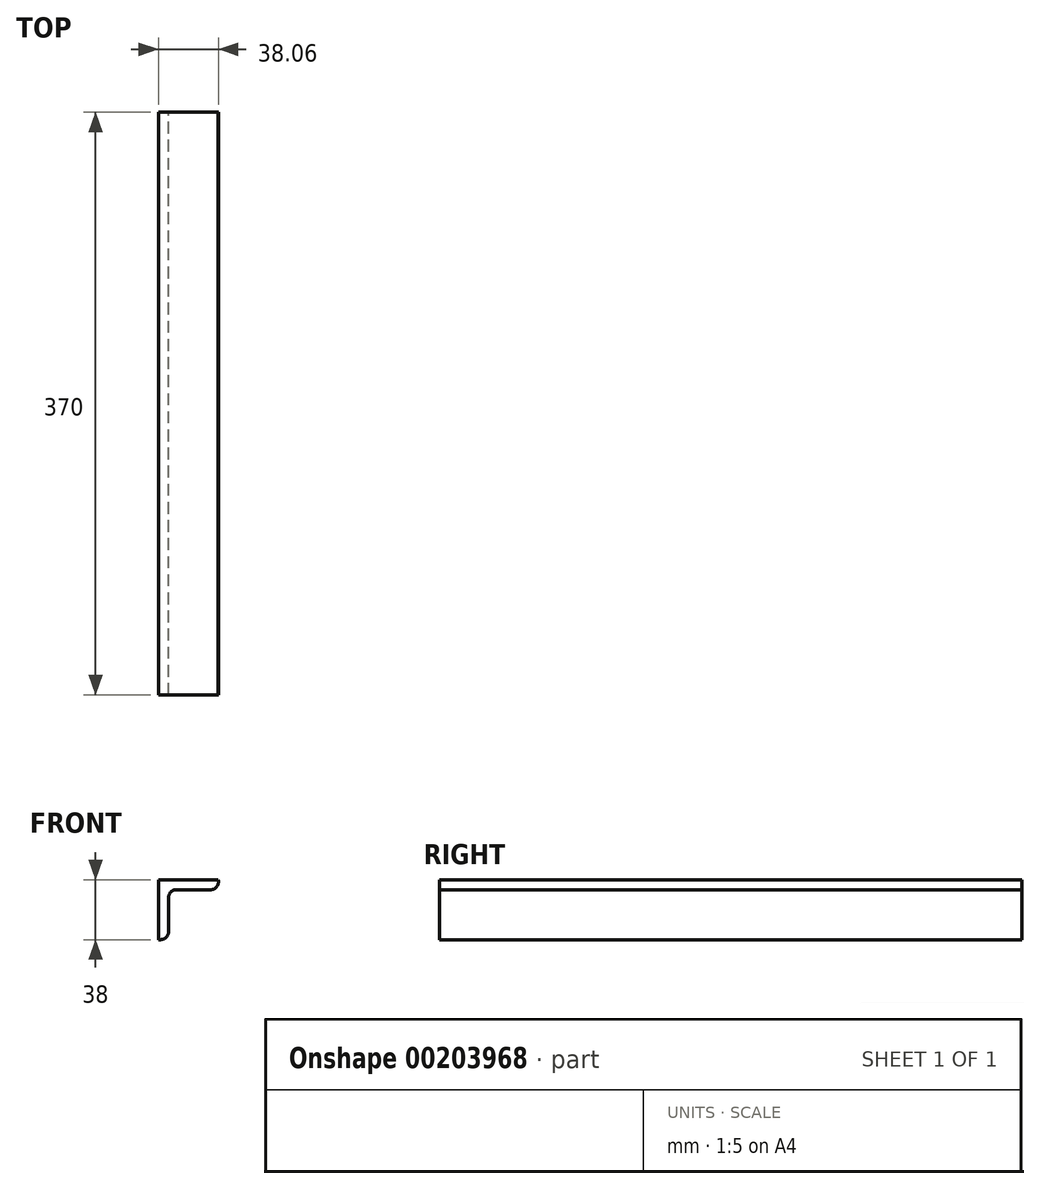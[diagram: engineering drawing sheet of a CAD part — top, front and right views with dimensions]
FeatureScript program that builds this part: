
annotation { "Feature Type Name" : "Feature", "Feature Type Description" : "" }
export const myFeature = defineFeature(function(context is Context, id is Id, definition is map)
    precondition{}
    {
        {
            var Q0;
            Q0=qCreatedBy(makeId("Front.planeOp"),FACE);
            var sketch = newSketch(context, id + "F0", { "sketchPlane" : qUnion([Q0])});
            skLineSegment(sketch, "E0", {"start": v(0, 0) * mm, "end": v(0, -38) * mm});
            skLineSegment(sketch, "E1", {"start": v(0, 0) * mm, "end": v(38, 0) * mm});
            skLineSegment(sketch, "E2", {"start": v(0, -38) * mm, "end": v(6.35, -38) * mm});
            skLineSegment(sketch, "E3", {"start": v(6.35, -38) * mm, "end": v(6.35, -6.34) * mm});
            skLineSegment(sketch, "E4", {"start": v(6.35, -6.34) * mm, "end": v(38.3, -6.34) * mm});
            skLineSegment(sketch, "E5", {"start": v(38.3, -6.34) * mm, "end": v(38, 0) * mm});
            skSolve(sketch);
        }
        {
            var Q0;
            Q0=makeQuery(id+"F0.imprint","IMPRINT",FACE,{"disambiguationData":[TD([[makeQuery(id+"F0.imprint","IMPRINT",EDGE,{"derivedFrom":sQuery(id+"F0.wireOp",EDGE,"E0")}),1.0]])]});
            extrude(context, id + "F1", {"entities" : qUnion([Q0]), "depth" : 370 * mm});
        }
        {
            var Q0;
            Q0=makeQuery(id+"F1.opExtrude","SWEPT_EDGE",EDGE,{"disambiguationData":[OSD([sQuery(id+"F0.wireOp",EDGE,"E2"),sQuery(id+"F0.wireOp",EDGE,"E3")])]});
            var Q1;
            Q1=makeQuery(id+"F1.opExtrude","SWEPT_EDGE",EDGE,{"disambiguationData":[OSD([sQuery(id+"F0.wireOp",EDGE,"E3"),sQuery(id+"F0.wireOp",EDGE,"E4")])]});
            fillet(context, id + "F2", {"entities" : qUnion([Q0, Q1]), "radius" : 5 * mm, "tangentPropagation" : true, "allowEdgeOverflow" : false});
        }
        {
            var Q0;
            Q0=makeQuery(id+"F1.opExtrude","SWEPT_EDGE",EDGE,{"disambiguationData":[OSD([sQuery(id+"F0.wireOp",EDGE,"E4"),sQuery(id+"F0.wireOp",EDGE,"E5")])]});
            fillet(context, id + "F3", {"entities" : qUnion([Q0]), "radius" : 5 * mm, "tangentPropagation" : true, "allowEdgeOverflow" : false});
        }
        {
            var Q0;
            Q0=makeQuery(id+"F1.opExtrude","SWEPT_FACE",FACE,{"disambiguationData":[OSD([sQuery(id+"F0.wireOp",EDGE,"E1")])]});
            var sketch = newSketch(context, id + "F4", { "sketchPlane" : qUnion([Q0])});
            skPoint(sketch, "E6", {"position": v(32, -29) * mm});
            skPoint(sketch, "E7", {"position": v(32, -133) * mm});
            skPoint(sketch, "E8", {"position": v(32, -237) * mm});
            skPoint(sketch, "E9", {"position": v(30.36, -341) * mm});
            skSolve(sketch);
        }
        {
            var Q0;
            {var subQ0=sQuery(id+"F0.wireOp",EDGE,"E1");Q0=makeQuery(id+"F4.imprint","IMPRINT",FACE,{"disambiguationData":[TD([[makeQuery(id+"F4.imprint","IMPRINT",EDGE,{"derivedFrom":makeQuery(id+"F1.opExtrude","CAP_EDGE",EDGE,{"disambiguationData":[OSD([subQ0])],"isStart":true})}),-1.0]])]});}
            var sketch = newSketch(context, id + "F5", { "sketchPlane" : qUnion([Q0])});
            skSolve(sketch);
        }
    });
